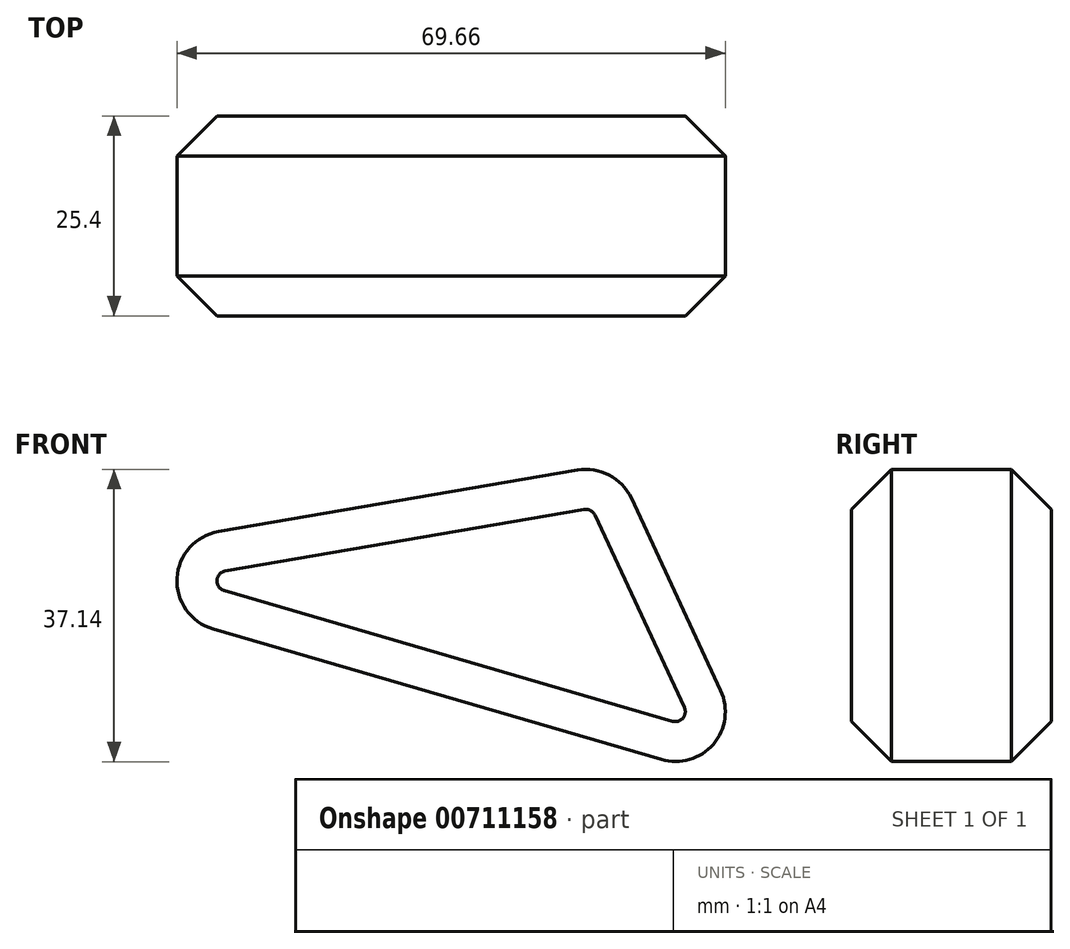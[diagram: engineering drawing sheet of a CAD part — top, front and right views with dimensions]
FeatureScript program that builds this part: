
annotation { "Feature Type Name" : "Feature", "Feature Type Description" : "" }
export const myFeature = defineFeature(function(context is Context, id is Id, definition is map)
    precondition{}
    {
        {
            var Q0;
            Q0=qCreatedBy(makeId("Front.planeOp"),FACE);
            var sketch = newSketch(context, id + "F0", { "sketchPlane" : qUnion([Q0])});
            skLineSegment(sketch, "E0", {"start": v(-19.3, 34.9) * mm, "end": v(37.66, 18.29) * mm});
            skLineSegment(sketch, "E1", {"start": v(45.2, 27.06) * mm, "end": v(33.84, 51.5) * mm});
            skLineSegment(sketch, "E2", {"start": v(27, 55.08) * mm, "end": v(-18.6, 47.25) * mm});
            skLineSegment(sketch, "E3", {"start": v(34.05, 215.1) * mm, "end": v(17.28, 215.1) * mm});
            skPoint(sketch, "E4.visualSharp", {"position": v(-45.7, 42.6) * mm});
            skArc(sketch, "E4.filletArc", {"start": v(-18.6, 47.25) * mm, "mid": v(-23.86, 41.35) * mm, "end": v(-19.3, 34.9) * mm});
            skPoint(sketch, "E5.visualSharp", {"position": v(51.1, 14.37) * mm});
            skArc(sketch, "E5.filletArc", {"start": v(37.66, 18.29) * mm, "mid": v(44.25, 20.24) * mm, "end": v(45.2, 27.06) * mm});
            skPoint(sketch, "E6.visualSharp", {"position": v(31.79, 55.9) * mm});
            skArc(sketch, "E6.filletArc", {"start": v(33.84, 51.5) * mm, "mid": v(31.03, 54.44) * mm, "end": v(27, 55.08) * mm});
            skSolve(sketch);
        }
        {
            var Q0;
            Q0 = qSketchRegion(id + "F0", true);
            extrude(context, id + "F1", {"entities" : qUnion([Q0]), "depth" : 25.4 * mm, "offsetDistance" : 25.4 * mm});
        }
        {
            var Q0;
            Q0=makeQuery(id+"F1.opExtrude","CAP_FACE",FACE,{"disambiguationData":[OSD([sQuery(id+"F0.wireOp",EDGE,"E0"),sQuery(id+"F0.wireOp",EDGE,"E1"),sQuery(id+"F0.wireOp",EDGE,"E2"),sQuery(id+"F0.wireOp",EDGE,"E4.filletArc"),sQuery(id+"F0.wireOp",EDGE,"E5.filletArc"),sQuery(id+"F0.wireOp",EDGE,"E6.filletArc")])],"isStart":true});
            var Q1;
            Q1=makeQuery(id+"F1.opExtrude","CAP_EDGE",EDGE,{"disambiguationData":[OSD([sQuery(id+"F0.wireOp",EDGE,"E0")])],"isStart":false});
            chamfer(context, id + "F2", {"entities" : qUnion([Q0, Q1]), "width" : 5.08 * mm, "tangentPropagation" : true});
        }
    });
